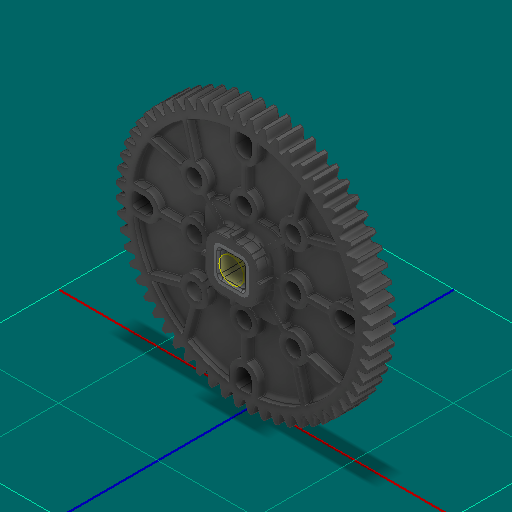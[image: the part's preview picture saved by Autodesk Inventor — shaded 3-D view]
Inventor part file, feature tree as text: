
AUTODESK INVENTOR PART (.ipt)
format: ipt  version: 2025 (Build 290162000, 162)  size: 4,823,552 bytes
history: native  units: in
note: dims shown in document units (in); Inventor stores cm internally (conversion verified against a paired STEP export)
features: other x6, sketch x3
ambient origin geometry x8: Origin, YZ Plane, XZ Plane, XY Plane, X Axis, Y Axis, Z Axis, Center Point
bodies: Solid1 (feature_tree), Solid2 (feature_tree)
feature tree (9):
  other  "Half Cut HS 60T Gear.ipt"
  other  "Solid1::Half Cut HS 60T Gear.ipt"
  other  "Solid2::Half Cut HS 60T Gear.ipt"
  other  "TaggingFeature1"
  sketch  "Sketch1"  dims[d0=0.3937in]
  sketch  "Sketch2"
  sketch  "Sketch3"
  other  "Srf1"
  other  "Srf1::Derived"
